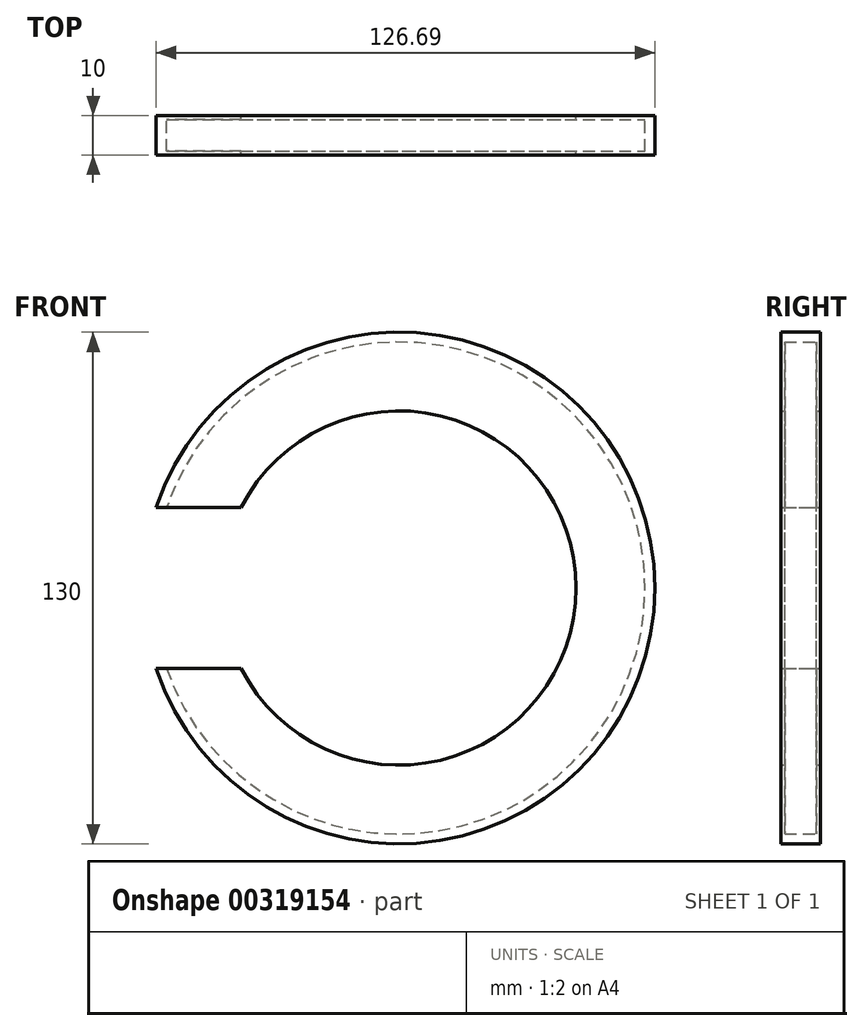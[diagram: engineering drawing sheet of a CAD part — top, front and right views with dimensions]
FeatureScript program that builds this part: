
annotation { "Feature Type Name" : "Feature", "Feature Type Description" : "" }
export const myFeature = defineFeature(function(context is Context, id is Id, definition is map)
    precondition{}
    {
        {
            var Q0;
            Q0=qCreatedBy(makeId("Front.planeOp"),FACE);
            var sketch = newSketch(context, id + "F0", { "sketchPlane" : qUnion([Q0])});
            skCircle(sketch, "E0", {"center": v(0, 0) * mm, "radius": 65 * mm});
            skSolve(sketch);
        }
        {
            var Q0;
            Q0=makeQuery(id+"F0.imprint","IMPRINT",FACE,{"disambiguationData":[TD([[makeQuery(id+"F0.imprint","IMPRINT",EDGE,{"derivedFrom":sQuery(id+"F0.wireOp",EDGE,"E0")}),1.0]])]});
            extrude(context, id + "F1", {"entities" : qUnion([Q0]), "depth" : 10 * mm});
        }
        {
            var Q0;
            Q0=qCreatedBy(makeId("Front.planeOp"),FACE);
            var sketch = newSketch(context, id + "F2", { "sketchPlane" : qUnion([Q0])});
            skArc(sketch, "E1", {"start": v(-40.07, -20.49) * mm, "mid": v(45, 0) * mm, "end": v(-40.07, 20.49) * mm});
            skLineSegment(sketch, "E2.bottom", {"start": v(-40.07, 20.49) * mm, "end": v(-167.12, 20.49) * mm});
            skLineSegment(sketch, "E2.top", {"start": v(-40.07, -20.49) * mm, "end": v(-104.8, -20.49) * mm});
            skLineSegment(sketch, "E2.right", {"start": v(-167.12, 20.49) * mm, "end": v(-104.8, -20.49) * mm});
            skPoint(sketch, "E2.middle", {"position": v(-68.77, 0) * mm});
            skPoint(sketch, "E2.left.end.orphan", {"position": v(29.57, -20.49) * mm});
            skPoint(sketch, "E3.orphan", {"position": v(-32.75, 20.49) * mm});
            skSolve(sketch);
        }
        {
            var Q0;
            Q0 = qSketchRegion(id + "F2", true);
            extrude(context, id + "F3", {"entities" : qUnion([Q0]), "operationType" : NewBodyOperationType.REMOVE, "endBound" : BoundingType.THROUGH_ALL, "depth" : 3 * mm});
        }
        {
            var Q0;
            Q0=qCreatedBy(makeId("Front.planeOp"),FACE);
            cPlane(context, id + "F4", {"entities" : qUnion([Q0]), "cplaneType" : CPlaneType.OFFSET, "offset" : 1 * mm, "width" : 150 * mm, "height" : 150 * mm});
        }
        {
            var Q0;
            Q0=qCreatedBy(id+"F4.planeOp",FACE);
            var sketch = newSketch(context, id + "F5", { "sketchPlane" : qUnion([Q0])});
            skCircle(sketch, "E4", {"center": v(0, 0) * mm, "radius": 62.5 * mm});
            skSolve(sketch);
        }
        {
            var Q0;
            Q0 = qSketchRegion(id + "F5", true);
            extrude(context, id + "F6", {"entities" : qUnion([Q0]), "operationType" : NewBodyOperationType.REMOVE, "depth" : 8 * mm});
        }
    });
